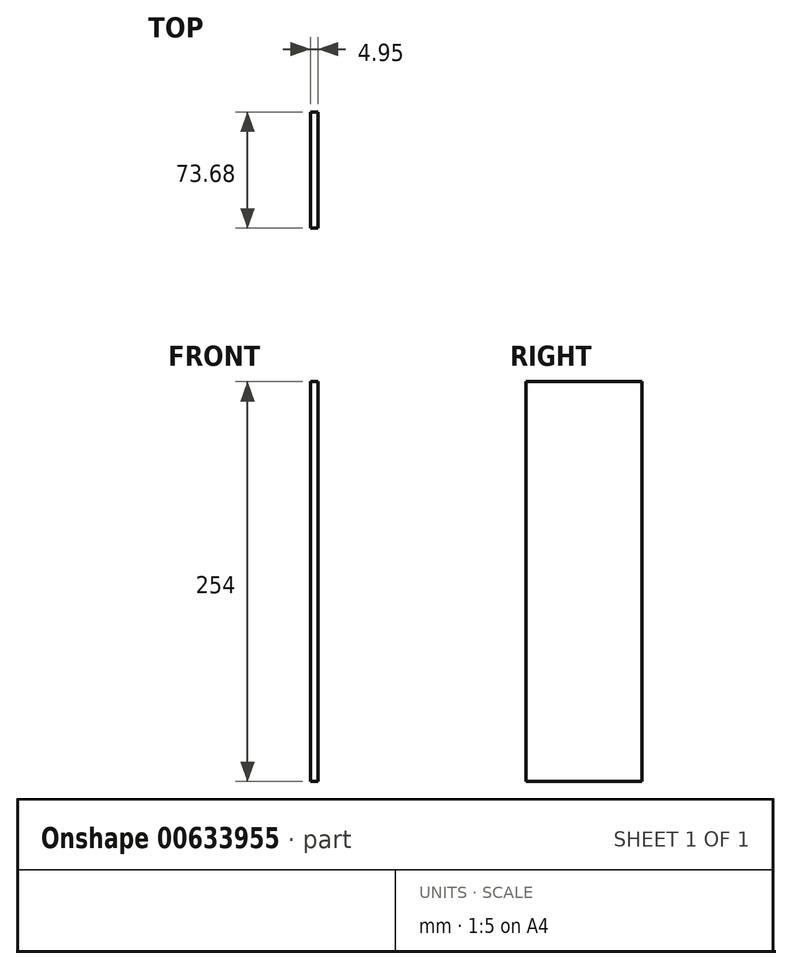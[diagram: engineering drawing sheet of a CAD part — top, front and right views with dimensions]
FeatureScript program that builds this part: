
annotation { "Feature Type Name" : "Feature", "Feature Type Description" : "" }
export const myFeature = defineFeature(function(context is Context, id is Id, definition is map)
    precondition{}
    {
        {
            var Q0;
            Q0=qCreatedBy(makeId("Top.planeOp"),FACE);
            var sketch = newSketch(context, id + "F0", { "sketchPlane" : qUnion([Q0])});
            skLineSegment(sketch, "E0.bottom", {"start": v(-32.38, 47.93) * mm, "end": v(-27.43, 47.93) * mm});
            skLineSegment(sketch, "E0.top", {"start": v(-32.38, -25.75) * mm, "end": v(-27.43, -25.75) * mm});
            skLineSegment(sketch, "E0.left", {"start": v(-32.38, 47.93) * mm, "end": v(-32.38, -25.75) * mm});
            skLineSegment(sketch, "E0.right", {"start": v(-27.43, 47.93) * mm, "end": v(-27.43, -25.75) * mm});
            skSolve(sketch);
        }
        {
            var Q0;
            Q0=makeQuery(id+"F0.imprint","IMPRINT",FACE,{"disambiguationData":[TD([[makeQuery(id+"F0.imprint","IMPRINT",EDGE,{"derivedFrom":sQuery(id+"F0.wireOp",EDGE,"E0.bottom")}),-1.0]])]});
            var sketch = newSketch(context, id + "F1", { "sketchPlane" : qUnion([Q0])});
            skSolve(sketch);
        }
        {
            var Q0;
            Q0=makeQuery(id+"F0.imprint","IMPRINT",FACE,{"disambiguationData":[TD([[makeQuery(id+"F0.imprint","IMPRINT",EDGE,{"derivedFrom":sQuery(id+"F0.wireOp",EDGE,"E0.bottom")}),-1.0]])]});
            var Q1;
            Q1=makeQuery(id+"F1.imprint","IMPRINT",FACE,{"disambiguationData":[TD([[makeQuery(id+"F1.imprint","IMPRINT",EDGE,{"derivedFrom":makeQuery(id+"F0.imprint","IMPRINT",EDGE,{"derivedFrom":sQuery(id+"F0.wireOp",EDGE,"E0.bottom")})}),-1.0]])]});
            extrude(context, id + "F2", {"entities" : qUnion([Q0, Q1]), "depth" : 254 * mm, "offsetDistance" : 25.4 * mm});
        }
    });
